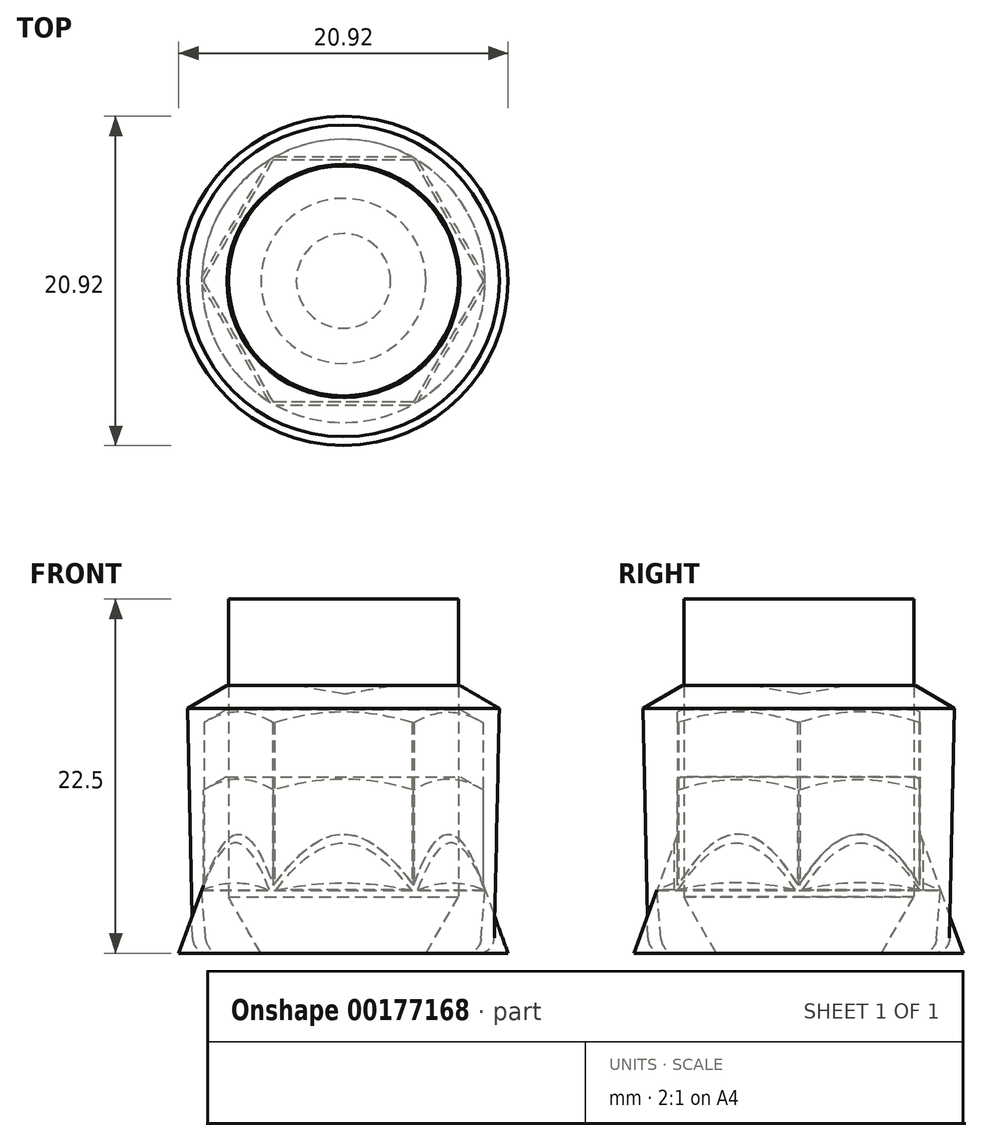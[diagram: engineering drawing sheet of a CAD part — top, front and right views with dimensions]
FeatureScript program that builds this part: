
annotation { "Feature Type Name" : "Feature", "Feature Type Description" : "" }
export const myFeature = defineFeature(function(context is Context, id is Id, definition is map)
    precondition{}
    {
        {
            var Q0;
            Q0=qCreatedBy(makeId("Front.planeOp"),FACE);
            var sketch = newSketch(context, id + "F0", { "sketchPlane" : qUnion([Q0])});
            skLineSegment(sketch, "E0", {"start": v(0, 0) * mm, "end": v(0, 11.2) * mm});
            skLineSegment(sketch, "E1", {"start": v(0, 11.2) * mm, "end": v(7.45, 11.2) * mm});
            skLineSegment(sketch, "E2", {"start": v(9.1, 10.25) * mm, "end": v(9.1, 3.97) * mm});
            skLineSegment(sketch, "E3", {"start": v(9.1, 3.97) * mm, "end": v(12.56, 2.5) * mm});
            skLineSegment(sketch, "E4", {"start": v(13, 2.31) * mm, "end": v(13, 0) * mm, "construction": true});
            skLineSegment(sketch, "E5", {"start": v(12.56, 0) * mm, "end": v(0, 0) * mm});
            skLineSegment(sketch, "E6", {"start": v(7.45, 11.2) * mm, "end": v(9.1, 10.25) * mm});
            skLineSegment(sketch, "E7", {"start": v(0, 0) * mm, "end": v(0, 11.2) * mm, "construction": true});
            skArc(sketch, "E8", {"start": v(12.56, 0) * mm, "mid": v(13, 1.25) * mm, "end": v(12.56, 2.5) * mm});
            skSolve(sketch);
        }
        {
            var Q0;
            Q0=qSketchRegion(id+"F0",true);
            var Q1;
            Q1=sQuery(id+"F0.wireOp",EDGE,"E0");
            revolve(context, id + "F1", {"entities" : qUnion([Q0]), "axis" : qUnion([Q1]), "revolveType" : RevolveType.FULL});
        }
        {
            var Q0;
            Q0=makeQuery(id+"F1.opRevolve","SWEPT_FACE",FACE,{"disambiguationData":[OSD([sQuery(id+"F0.wireOp",EDGE,"E1")])]});
            var sketch = newSketch(context, id + "F2", { "sketchPlane" : qUnion([Q0])});
            skCircle(sketch, "E9.cCircle", {"center": v(0, 0) * mm, "radius": 7.9 * mm, "construction": true});
            skLineSegment(sketch, "E9.0", {"start": v(-4.56, 7.9) * mm, "end": v(4.56, 7.9) * mm});
            skLineSegment(sketch, "E9.1", {"start": v(4.56, 7.9) * mm, "end": v(9.13, 0) * mm});
            skLineSegment(sketch, "E9.2", {"start": v(9.13, 0) * mm, "end": v(4.56, -7.9) * mm});
            skLineSegment(sketch, "E9.3", {"start": v(4.56, -7.9) * mm, "end": v(-4.56, -7.9) * mm});
            skLineSegment(sketch, "E9.4", {"start": v(-4.56, -7.9) * mm, "end": v(-9.13, 0) * mm});
            skLineSegment(sketch, "E9.5", {"start": v(-9.13, 0) * mm, "end": v(-4.56, 7.9) * mm});
            skPoint(sketch, "E9.0.midPoint", {"position": v(0, 7.9) * mm});
            skCircle(sketch, "E10", {"center": v(0, 0) * mm, "radius": 15.35 * mm});
            skSolve(sketch);
        }
        {
            var Q0;
            Q0=qSketchRegion(id+"F2",true);
            var Q1;
            Q1=makeQuery(id+"F1.opRevolve","SWEPT_FACE",FACE,{"disambiguationData":[OSD([sQuery(id+"F0.wireOp",EDGE,"E3")])]});
            extrude(context, id + "F3", {"entities" : qUnion([Q0]), "operationType" : NewBodyOperationType.REMOVE, "endBound" : BoundingType.UP_TO_SURFACE, "oppositeDirection" : true, "endBoundEntityFace" : qUnion([Q1]), "depth" : 25 * mm, "offsetDistance" : 25 * mm});
        }
        {
            var Q0;
            Q0=qCreatedBy(makeId("Front.planeOp"),FACE);
            var sketch = newSketch(context, id + "F4", { "sketchPlane" : qUnion([Q0])});
            skLineSegment(sketch, "E11", {"start": v(0, 0) * mm, "end": v(0, 15.5) * mm});
            skLineSegment(sketch, "E12", {"start": v(0, 15.5) * mm, "end": v(7.4, 15.5) * mm});
            skLineSegment(sketch, "E13", {"start": v(8.85, 14.66) * mm, "end": v(8.85, 4.41) * mm});
            skLineSegment(sketch, "E14", {"start": v(8.85, 4.41) * mm, "end": v(9, 4) * mm});
            skLineSegment(sketch, "E15", {"start": v(7.75, 0) * mm, "end": v(0, 0) * mm});
            skLineSegment(sketch, "E16", {"start": v(7.4, 15.5) * mm, "end": v(8.85, 14.66) * mm});
            skLineSegment(sketch, "E17", {"start": v(0, 0) * mm, "end": v(0, 15.5) * mm, "construction": true});
            skLineSegment(sketch, "E18", {"start": v(9, 4) * mm, "end": v(8.75, 0.92) * mm});
            skPoint(sketch, "E19.visualSharp", {"position": v(8.68, 0) * mm});
            skArc(sketch, "E19.filletArc", {"start": v(7.75, 0) * mm, "mid": v(8.43, 0.26) * mm, "end": v(8.75, 0.92) * mm});
            skSolve(sketch);
        }
        {
            var Q0;
            Q0 = qSketchRegion(id + "F4", true);
            var Q1;
            Q1=sQuery(id+"F4.wireOp",EDGE,"E11");
            revolve(context, id + "F5", {"surfaceOperationType" : NewSurfaceOperationType.NEW, "entities" : qUnion([Q0]), "axis" : qUnion([Q1]), "revolveType" : RevolveType.FULL});
        }
        {
            var Q0;
            Q0=makeQuery(id+"F5.opRevolve","SWEPT_FACE",FACE,{"disambiguationData":[OSD([sQuery(id+"F4.wireOp",EDGE,"E12")])]});
            var sketch = newSketch(context, id + "F6", { "sketchPlane" : qUnion([Q0])});
            skCircle(sketch, "E20.cCircle", {"center": v(0, 0) * mm, "radius": 7.7 * mm, "construction": true});
            skLineSegment(sketch, "E20.0", {"start": v(-4.45, 7.7) * mm, "end": v(4.45, 7.7) * mm});
            skLineSegment(sketch, "E20.1", {"start": v(4.45, 7.7) * mm, "end": v(8.9, 0) * mm});
            skLineSegment(sketch, "E20.2", {"start": v(8.9, 0) * mm, "end": v(4.45, -7.7) * mm});
            skLineSegment(sketch, "E20.3", {"start": v(4.45, -7.7) * mm, "end": v(-4.45, -7.7) * mm});
            skLineSegment(sketch, "E20.4", {"start": v(-4.45, -7.7) * mm, "end": v(-8.9, 0) * mm});
            skLineSegment(sketch, "E20.5", {"start": v(-8.9, 0) * mm, "end": v(-4.45, 7.7) * mm});
            skPoint(sketch, "E20.0.midPoint", {"position": v(0, 7.7) * mm});
            skCircle(sketch, "E21", {"center": v(0, 0) * mm, "radius": 14.95 * mm});
            skSolve(sketch);
        }
        {
            var Q0;
            Q0 = qSketchRegion(id + "F6", true);
            var Q1;
            Q1=makeQuery(id+"F5.opRevolve","SWEPT_FACE",FACE,{"disambiguationData":[OSD([sQuery(id+"F4.wireOp",EDGE,"E14")])]});
            extrude(context, id + "F7", {"entities" : qUnion([Q0]), "operationType" : NewBodyOperationType.REMOVE, "endBound" : BoundingType.UP_TO_SURFACE, "oppositeDirection" : true, "depth" : 25 * mm, "endBoundEntityFace" : qUnion([Q1]), "offsetDistance" : 25 * mm});
        }
        {
            var Q0;
            Q0=qCreatedBy(makeId("Front.planeOp"),FACE);
            var sketch = newSketch(context, id + "F8", { "sketchPlane" : qUnion([Q0])});
            skLineSegment(sketch, "E22", {"start": v(0, 0) * mm, "end": v(0, 16.47) * mm, "construction": true});
            skLineSegment(sketch, "E23", {"start": v(3, 17) * mm, "end": v(7.4, 17) * mm});
            skLineSegment(sketch, "E24", {"start": v(7.4, 17) * mm, "end": v(9.9, 15.56) * mm});
            skLineSegment(sketch, "E25", {"start": v(8.58, 0) * mm, "end": v(0, 0) * mm});
            skLineSegment(sketch, "E26", {"start": v(0, 16.47) * mm, "end": v(0, 0) * mm});
            skLineSegment(sketch, "E27", {"start": v(9.9, 15.56) * mm, "end": v(9.58, 0.98) * mm});
            skPoint(sketch, "E28.visualSharp", {"position": v(9.56, 0) * mm});
            skArc(sketch, "E28.filletArc", {"start": v(8.58, 0) * mm, "mid": v(9.28, 0.29) * mm, "end": v(9.58, 0.98) * mm});
            skLineSegment(sketch, "E29", {"start": v(3, 17) * mm, "end": v(0, 16.47) * mm});
            skSolve(sketch);
        }
        {
            var Q0;
            Q0=qSketchRegion(id+"F8",true);
            var Q1;
            Q1=sQuery(id+"F8.wireOp",EDGE,"E26");
            revolve(context, id + "F9", {"surfaceOperationType" : NewSurfaceOperationType.NEW, "entities" : qUnion([Q0]), "axis" : qUnion([Q1]), "revolveType" : RevolveType.FULL});
        }
        {
            var Q0;
            Q0=qCreatedBy(makeId("Front.planeOp"),FACE);
            var sketch = newSketch(context, id + "F10", { "sketchPlane" : qUnion([Q0])});
            skLineSegment(sketch, "E30", {"start": v(0, 0) * mm, "end": v(0, 22.5) * mm});
            skLineSegment(sketch, "E31", {"start": v(0, 22.5) * mm, "end": v(7.3, 22.5) * mm});
            skLineSegment(sketch, "E32", {"start": v(7.3, 22.5) * mm, "end": v(7.3, 3.57) * mm});
            skLineSegment(sketch, "E33", {"start": v(7.3, 3.57) * mm, "end": v(5.24, 0) * mm});
            skLineSegment(sketch, "E34", {"start": v(5.24, 0) * mm, "end": v(0, 0) * mm});
            skLineSegment(sketch, "E35", {"start": v(0, 22.5) * mm, "end": v(0, 0) * mm, "construction": true});
            skSolve(sketch);
        }
        {
            var Q0;
            Q0=qSketchRegion(id+"F10",true);
            var Q1;
            Q1=sQuery(id+"F10.wireOp",EDGE,"E30");
            revolve(context, id + "F11", {"surfaceOperationType" : NewSurfaceOperationType.NEW, "entities" : qUnion([Q0]), "axis" : qUnion([Q1]), "revolveType" : RevolveType.FULL});
        }
    });
